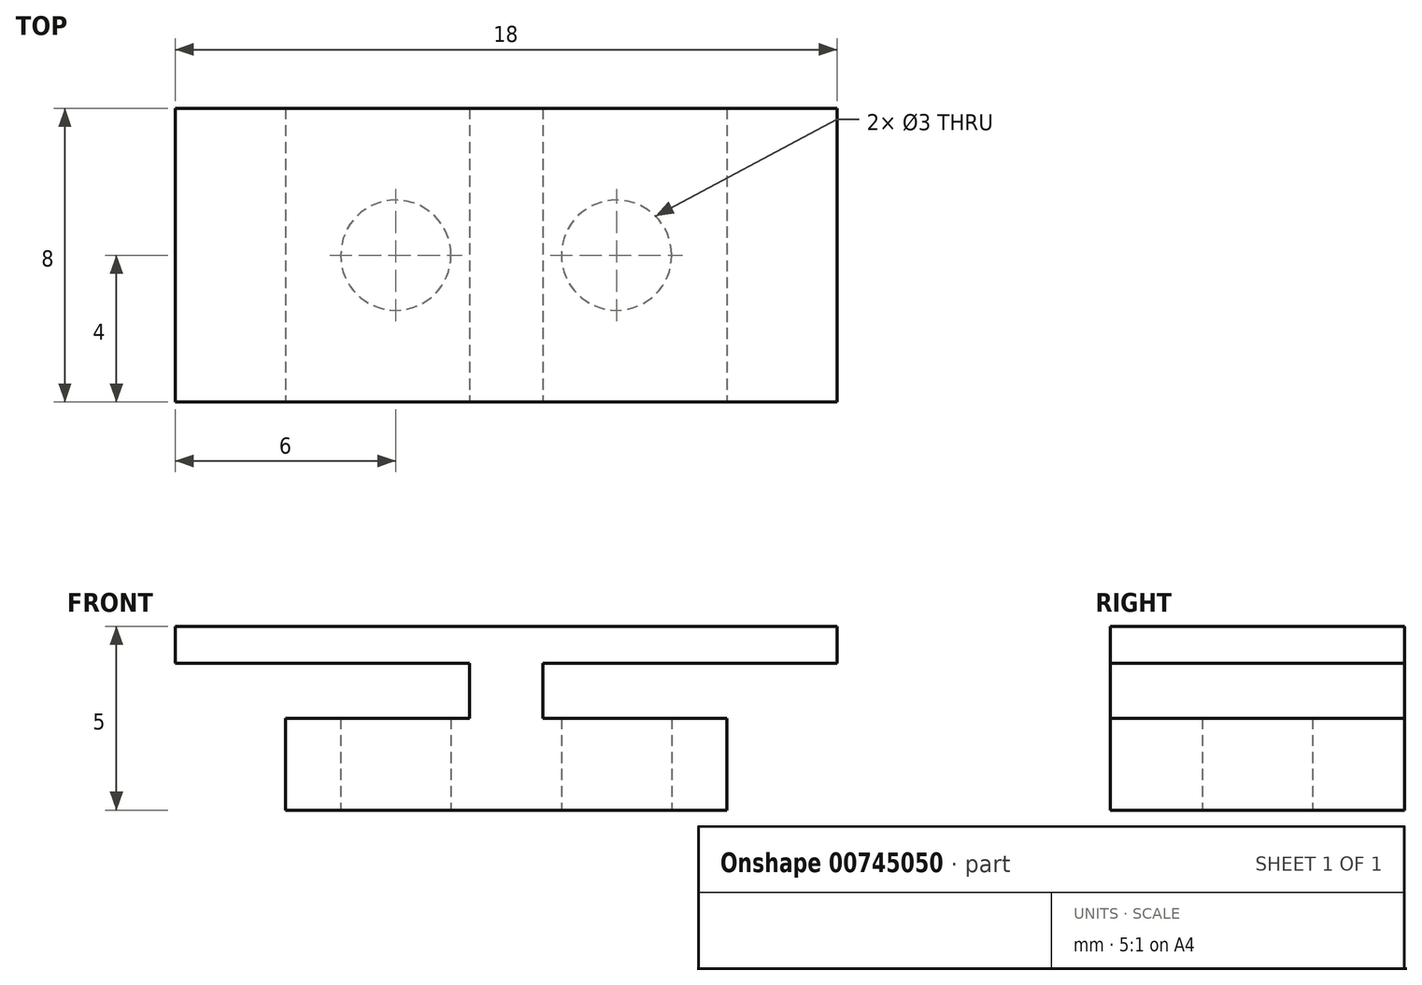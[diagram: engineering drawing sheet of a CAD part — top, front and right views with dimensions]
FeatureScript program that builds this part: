
annotation { "Feature Type Name" : "Feature", "Feature Type Description" : "" }
export const myFeature = defineFeature(function(context is Context, id is Id, definition is map)
    precondition{}
    {
        {
            var Q0;
            Q0=qCreatedBy(makeId("Top.planeOp"),FACE);
            var sketch = newSketch(context, id + "F0", { "sketchPlane" : qUnion([Q0])});
            skLineSegment(sketch, "E0.bottom", {"start": v(6, 4) * mm, "end": v(-6, 4) * mm});
            skLineSegment(sketch, "E0.top", {"start": v(6, -4) * mm, "end": v(-6, -4) * mm});
            skLineSegment(sketch, "E0.left", {"start": v(6, 4) * mm, "end": v(6, -4) * mm});
            skLineSegment(sketch, "E0.right", {"start": v(-6, 4) * mm, "end": v(-6, -4) * mm});
            skPoint(sketch, "E0.middle", {"position": v(0, 0) * mm});
            skLineSegment(sketch, "E1", {"start": v(-1, 4) * mm, "end": v(-1, -4) * mm});
            skLineSegment(sketch, "E2.MirrorCS", {"start": v(1, 4) * mm, "end": v(1, -4) * mm});
            skCircle(sketch, "E3", {"center": v(-3, 0) * mm, "radius": 1.5 * mm});
            skCircle(sketch, "E4.MirrorC", {"center": v(3, 0) * mm, "radius": 1.5 * mm});
            skSolve(sketch);
        }
        {
            var Q0;
            {var subQ0=sQuery(id+"F0.wireOp",EDGE,"E0.right");Q0=makeQuery(id+"F0.imprint","IMPRINT",FACE,{"disambiguationData":[TD([[makeQuery(id+"F0.imprint","IMPRINT",EDGE,{"derivedFrom":subQ0}),1.0]])]});}
            var Q1;
            {var subQ0=sQuery(id+"F0.wireOp",EDGE,"E0.left");Q1=makeQuery(id+"F0.imprint","IMPRINT",FACE,{"disambiguationData":[TD([[makeQuery(id+"F0.imprint","IMPRINT",EDGE,{"derivedFrom":subQ0}),-1.0]])]});}
            extrude(context, id + "F1", {"entities" : qUnion([Q0, Q1]), "depth" : 0.5 * mm, "offsetDistance" : 25 * mm});
        }
        {
            var Q0;
            {var subQ0=sQuery(id+"F0.wireOp",EDGE,"E1");Q0=makeQuery(id+"F0.imprint","IMPRINT",FACE,{"disambiguationData":[TD([[makeQuery(id+"F0.imprint","IMPRINT",EDGE,{"derivedFrom":subQ0}),1.0]])]});}
            extrude(context, id + "F2", {"entities" : qUnion([Q0]), "operationType" : NewBodyOperationType.ADD, "depth" : 2 * mm, "offsetDistance" : 25 * mm});
        }
        {
            var Q0;
            Q0=qCreatedBy(makeId("Top.planeOp"),FACE);
            cPlane(context, id + "F3", {"entities" : qUnion([Q0]), "cplaneType" : CPlaneType.OFFSET, "offset" : 2 * mm, "width" : 150 * mm, "height" : 150 * mm});
        }
        {
            var Q0;
            Q0=qCreatedBy(id+"F3.planeOp",FACE);
            var sketch = newSketch(context, id + "F4", { "sketchPlane" : qUnion([Q0])});
            skLineSegment(sketch, "E5.bottom", {"start": v(9, 4) * mm, "end": v(-9, 4) * mm});
            skLineSegment(sketch, "E5.top", {"start": v(9, -4) * mm, "end": v(-9, -4) * mm});
            skLineSegment(sketch, "E5.left", {"start": v(9, 4) * mm, "end": v(9, -4) * mm});
            skLineSegment(sketch, "E5.right", {"start": v(-9, 4) * mm, "end": v(-9, -4) * mm});
            skPoint(sketch, "E5.middle", {"position": v(0, 0) * mm});
            skSolve(sketch);
        }
        {
            var Q0;
            Q0=makeQuery(id+"F4.imprint","IMPRINT",FACE,{"disambiguationData":[TD([[makeQuery(id+"F4.imprint","IMPRINT",EDGE,{"derivedFrom":sQuery(id+"F4.wireOp",EDGE,"E5.bottom")}),1.0]])]});
            extrude(context, id + "F5", {"entities" : qUnion([Q0]), "operationType" : NewBodyOperationType.ADD, "depth" : 1 * mm, "offsetDistance" : 25 * mm});
        }
        {
            var Q0;
            {var subQ1=sQuery(id+"F0.wireOp",EDGE,"E0.right");Q0=makeQuery(id+"F0.imprint","IMPRINT",FACE,{"disambiguationData":[TD([[makeQuery(id+"F0.imprint","IMPRINT",EDGE,{"derivedFrom":subQ1}),1.0]])]});}
            var Q1;
            {var subQ0=sQuery(id+"F0.wireOp",EDGE,"E1");Q1=makeQuery(id+"F0.imprint","IMPRINT",FACE,{"disambiguationData":[TD([[makeQuery(id+"F0.imprint","IMPRINT",EDGE,{"derivedFrom":subQ0}),1.0]])]});}
            var Q2;
            {var subQ1=sQuery(id+"F0.wireOp",EDGE,"E0.left");Q2=makeQuery(id+"F0.imprint","IMPRINT",FACE,{"disambiguationData":[TD([[makeQuery(id+"F0.imprint","IMPRINT",EDGE,{"derivedFrom":subQ1}),-1.0]])]});}
            extrude(context, id + "F6", {"entities" : qUnion([Q0, Q1, Q2]), "operationType" : NewBodyOperationType.ADD, "oppositeDirection" : true, "depth" : 2 * mm, "offsetDistance" : 25 * mm});
        }
    });
